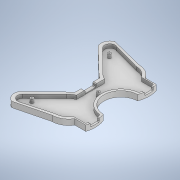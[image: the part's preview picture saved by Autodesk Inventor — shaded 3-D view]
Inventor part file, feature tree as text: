
AUTODESK INVENTOR PART (.ipt)
format: ipt  version: 2021 (Build 250183000, 183)  size: 271,872 bytes
history: native  units: mm
features: extrude x4, sketch x4, fillet x2, other x1
ambient origin geometry x8: Origin, YZ Plane, XZ Plane, XY Plane, X Axis, Y Axis, Z Axis, Center Point
bodies: Body1 (feature_tree)
feature tree (11):
  other  "Sólido1"
  extrude  "Extrusión1"  Depth=75.0mm
  extrude  "Extrusión2"  Depth=9.0mm
  extrude  "Extrusión3"  Depth=10.0mm
  fillet  "Empalme1"  Radius=10.0mm
  extrude  "Extrusión4"  Depth=2.0mm
  fillet  "Empalme2"  Radius=15.0mm
  sketch  "Boceto1"  dims[d3=75.0mm d4=75.0mm]
  sketch  "Boceto2"  dims[d7=135.0mm d8=9.0mm]
  sketch  "Boceto3"  dims[d9=9.0mm d10=9.0mm d11=10.0mm d12=0.0mm]
  sketch  "Boceto4"  dims[d13=5.0mm d14=0.0mm d15=15.0mm d16=15.0mm d17=8.0mm d18=15.0mm d19=0.0mm d20=2.0mm d21=8.0mm d22=0.0mm d23=2.0mm d24=0.872665mm]
